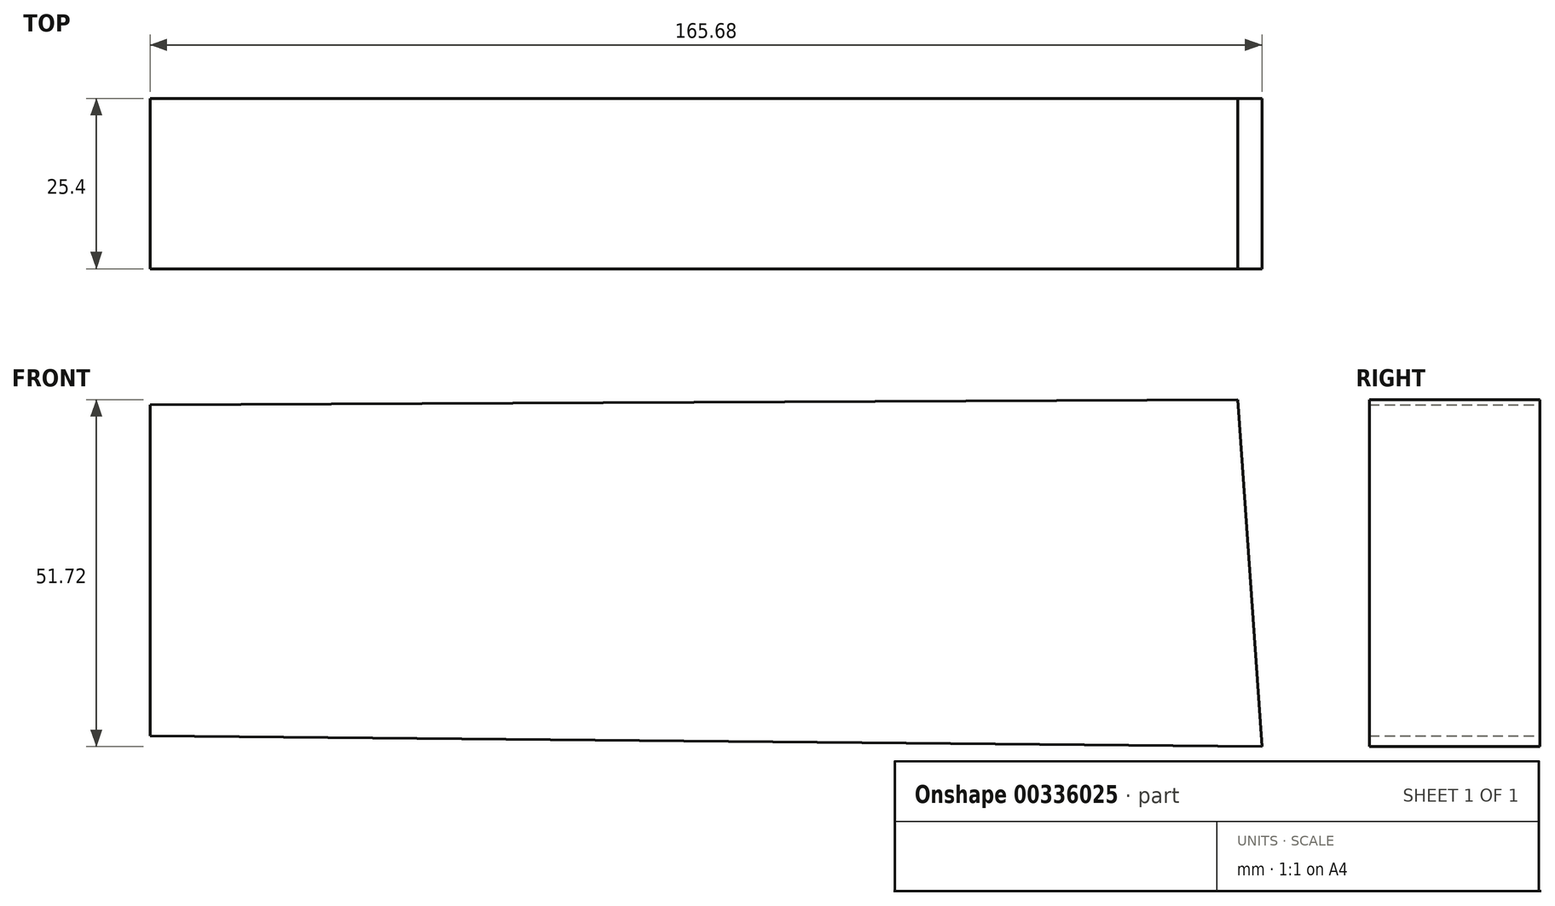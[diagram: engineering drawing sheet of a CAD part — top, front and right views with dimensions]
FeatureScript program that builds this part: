
annotation { "Feature Type Name" : "Feature", "Feature Type Description" : "" }
export const myFeature = defineFeature(function(context is Context, id is Id, definition is map)
    precondition{}
    {
        {
            var Q0;
            Q0=qCreatedBy(makeId("Front.planeOp"),FACE);
            var sketch = newSketch(context, id + "F0", { "sketchPlane" : qUnion([Q0])});
            skLineSegment(sketch, "E0", {"start": v(-64.25, 65.87) * mm, "end": v(-64.25, 16.57) * mm});
            skLineSegment(sketch, "E1", {"start": v(-64.25, 16.57) * mm, "end": v(101.43, 14.95) * mm});
            skLineSegment(sketch, "E2", {"start": v(101.43, 14.95) * mm, "end": v(97.8, 66.67) * mm});
            skLineSegment(sketch, "E3", {"start": v(97.8, 66.67) * mm, "end": v(-64.25, 65.87) * mm});
            skSolve(sketch);
        }
        {
            var Q0;
            Q0=makeQuery(id+"F0.imprint","IMPRINT",FACE,{"disambiguationData":[TD([[makeQuery(id+"F0.imprint","IMPRINT",EDGE,{"derivedFrom":sQuery(id+"F0.wireOp",EDGE,"E0")}),1.0]])]});
            extrude(context, id + "F1", {"entities" : qUnion([Q0]), "depth" : 25.4 * mm});
        }
    });
